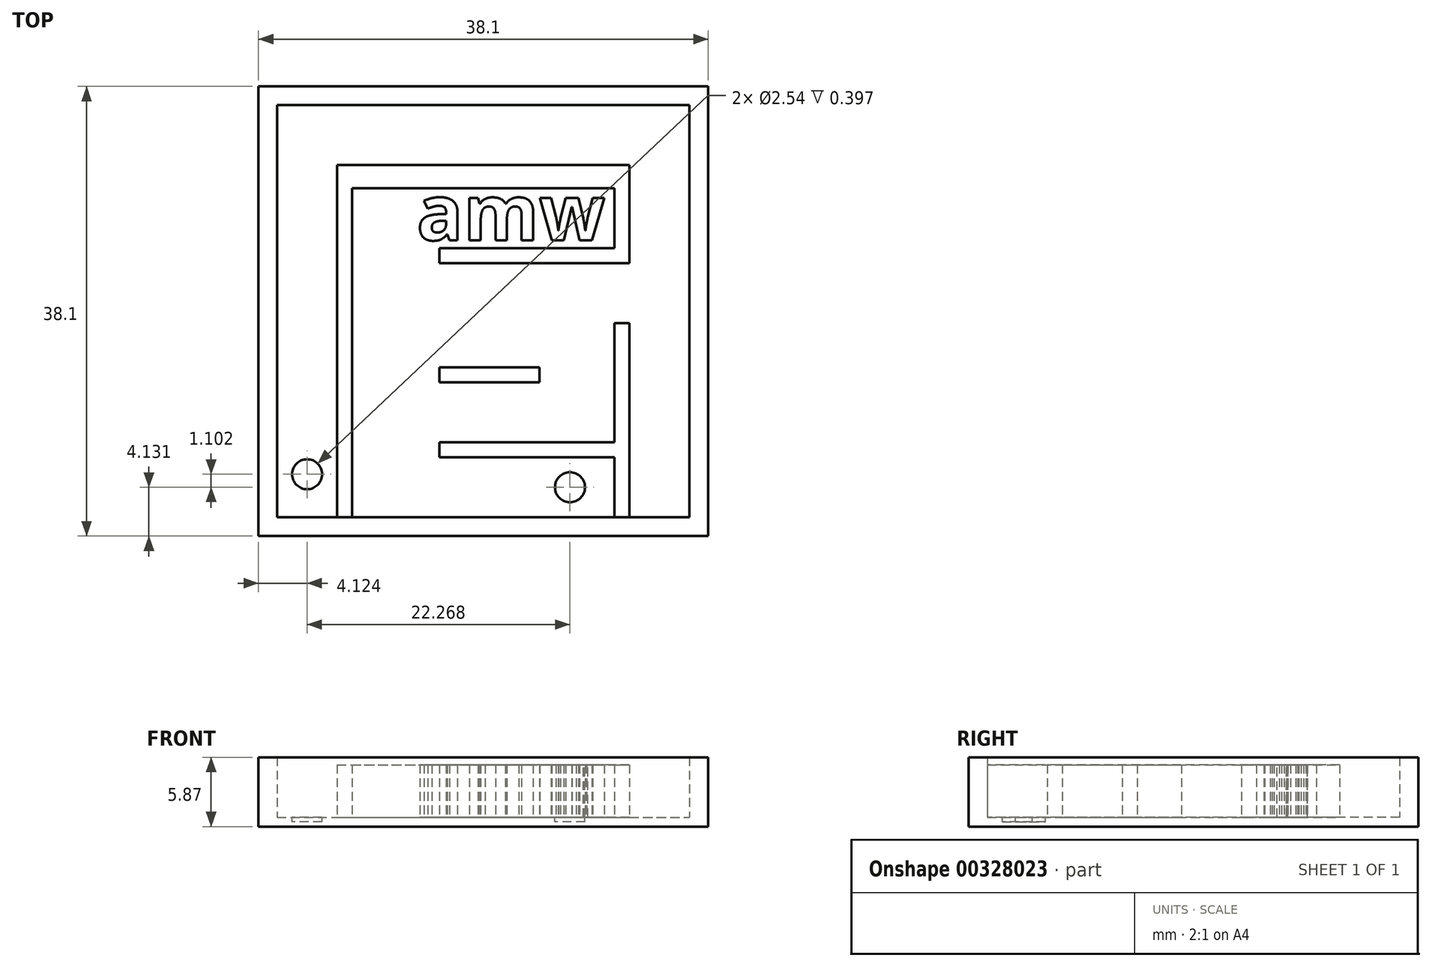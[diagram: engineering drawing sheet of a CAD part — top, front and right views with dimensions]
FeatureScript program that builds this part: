
annotation { "Feature Type Name" : "Feature", "Feature Type Description" : "" }
export const myFeature = defineFeature(function(context is Context, id is Id, definition is map)
    precondition{}
    {
        {
            var Q0;
            Q0=qCreatedBy(makeId("Top.planeOp"),FACE);
            var sketch = newSketch(context, id + "F0", { "sketchPlane" : qUnion([Q0])});
            skLineSegment(sketch, "E0.bottom", {"start": v(-17.87, 4.8) * mm, "end": v(20.23, 4.8) * mm});
            skLineSegment(sketch, "E0.top", {"start": v(-17.87, -33.3) * mm, "end": v(20.23, -33.3) * mm});
            skLineSegment(sketch, "E0.left", {"start": v(-17.87, 4.8) * mm, "end": v(-17.87, -33.3) * mm});
            skLineSegment(sketch, "E0.right", {"start": v(20.23, 4.8) * mm, "end": v(20.23, -33.3) * mm});
            skSolve(sketch);
        }
        {
            var Q0;
            Q0=makeQuery(id+"F0.imprint","IMPRINT",FACE,{"disambiguationData":[TD([[makeQuery(id+"F0.imprint","IMPRINT",EDGE,{"derivedFrom":sQuery(id+"F0.wireOp",EDGE,"E0.bottom")}),-1.0]])]});
            extrude(context, id + "F1", {"entities" : qUnion([Q0]), "depth" : 0.8 * mm});
        }
        {
            var Q0;
            Q0=makeQuery(id+"F1.opExtrude","CAP_FACE",FACE,{"disambiguationData":[OSD([sQuery(id+"F0.wireOp",EDGE,"E0.bottom"),sQuery(id+"F0.wireOp",EDGE,"E0.top"),sQuery(id+"F0.wireOp",EDGE,"E0.left"),sQuery(id+"F0.wireOp",EDGE,"E0.right")])],"isStart":false});
            var sketch = newSketch(context, id + "F2", { "sketchPlane" : qUnion([Q0])});
            skLineSegment(sketch, "E1.0", {"start": v(-16.29, 3.22) * mm, "end": v(18.64, 3.22) * mm});
            skLineSegment(sketch, "E1.1", {"start": v(-16.29, 3.22) * mm, "end": v(-16.29, -31.7) * mm});
            skLineSegment(sketch, "E1.2", {"start": v(-16.29, -31.7) * mm, "end": v(18.64, -31.7) * mm});
            skLineSegment(sketch, "E1.3", {"start": v(18.64, 3.22) * mm, "end": v(18.64, -31.7) * mm});
            skSolve(sketch);
        }
        {
            var Q0;
            Q0=makeQuery(id+"F2.imprint","IMPRINT",FACE,{"disambiguationData":[TD([[makeQuery(id+"F2.imprint","IMPRINT",EDGE,{"derivedFrom":sQuery(id+"F2.wireOp",EDGE,"E1.0")}),1.0]])]});
            extrude(context, id + "F3", {"entities" : qUnion([Q0]), "operationType" : NewBodyOperationType.ADD, "depth" : 5.08 * mm});
        }
        {
            var Q0;
            Q0=makeQuery(id+"F1.opExtrude","CAP_FACE",FACE,{"disambiguationData":[OSD([sQuery(id+"F0.wireOp",EDGE,"E0.bottom"),sQuery(id+"F0.wireOp",EDGE,"E0.top"),sQuery(id+"F0.wireOp",EDGE,"E0.left"),sQuery(id+"F0.wireOp",EDGE,"E0.right")])],"isStart":false});
            var sketch = newSketch(context, id + "F4", { "sketchPlane" : qUnion([Q0])});
            skLineSegment(sketch, "E2.bottom", {"start": v(-11.2, -31.7) * mm, "end": v(-9.94, -31.7) * mm});
            skLineSegment(sketch, "E2.top", {"start": v(-11.2, -1.86) * mm, "end": v(-9.94, -1.86) * mm});
            skLineSegment(sketch, "E2.left", {"start": v(-11.2, -31.7) * mm, "end": v(-11.2, -1.86) * mm});
            skLineSegment(sketch, "E3", {"start": v(-9.94, -1.86) * mm, "end": v(-9.94, -31.7) * mm});
            skLineSegment(sketch, "E4.left", {"start": v(13.56, -1.86) * mm, "end": v(13.56, -3.82) * mm});
            skPoint(sketch, "E5.oppositeSnap0", {"position": v(-11.2, -16.79) * mm});
            skLineSegment(sketch, "E5.right", {"start": v(-9.94, -20.38) * mm, "end": v(-9.94, -16.79) * mm});
            skLineSegment(sketch, "E6", {"start": v(-16.29, -31.7) * mm, "end": v(-11.2, -31.7) * mm});
            skCircle(sketch, "E7", {"center": v(-13.75, -28.07) * mm, "radius": 1.27 * mm});
            skPoint(sketch, "E7.centerSnap0", {"position": v(-13.75, -31.7) * mm});
            skPoint(sketch, "E8.orphan", {"position": v(-9.94, -1.86) * mm});
            skLineSegment(sketch, "E9.bottom", {"start": v(-9.94, -1.86) * mm, "end": v(13.56, -1.86) * mm});
            skLineSegment(sketch, "E9.top", {"start": v(-9.94, -3.82) * mm, "end": v(13.56, -3.82) * mm});
            skLineSegment(sketch, "E9.left", {"start": v(-9.94, -1.86) * mm, "end": v(-9.94, -3.82) * mm});
            skLineSegment(sketch, "E10", {"start": v(-9.94, -25.04) * mm, "end": v(-9.94, -31.7) * mm});
            skPoint(sketch, "E11.centerSnap0", {"position": v(-9.94, -28.38) * mm});
            skLineSegment(sketch, "E12.bottom", {"start": v(13.56, -1.86) * mm, "end": v(12.29, -1.86) * mm});
            skLineSegment(sketch, "E12.top", {"start": v(13.56, -10.17) * mm, "end": v(12.29, -10.17) * mm});
            skLineSegment(sketch, "E12.left", {"start": v(13.56, -1.86) * mm, "end": v(13.56, -10.17) * mm});
            skLineSegment(sketch, "E12.right", {"start": v(12.29, -1.86) * mm, "end": v(12.29, -10.17) * mm});
            skLineSegment(sketch, "E13.bottom", {"start": v(12.29, -31.7) * mm, "end": v(13.56, -31.7) * mm});
            skLineSegment(sketch, "E13.left", {"start": v(12.29, -31.7) * mm, "end": v(12.29, -26.63) * mm});
            skLineSegment(sketch, "E13.right", {"start": v(13.56, -31.7) * mm, "end": v(13.56, -25.36) * mm});
            skLineSegment(sketch, "E14.bottom", {"start": v(12.29, -10.17) * mm, "end": v(-2.54, -10.17) * mm});
            skLineSegment(sketch, "E14.top", {"start": v(12.29, -8.9) * mm, "end": v(-2.54, -8.9) * mm});
            skLineSegment(sketch, "E14.left", {"start": v(12.29, -10.17) * mm, "end": v(12.29, -8.9) * mm});
            skLineSegment(sketch, "E14.right", {"start": v(-2.54, -10.17) * mm, "end": v(-2.54, -8.9) * mm});
            skLineSegment(sketch, "E15.bottom", {"start": v(12.29, -25.36) * mm, "end": v(-2.54, -25.36) * mm});
            skLineSegment(sketch, "E15.top", {"start": v(12.29, -26.63) * mm, "end": v(-2.54, -26.63) * mm});
            skLineSegment(sketch, "E15.right", {"start": v(-2.54, -25.36) * mm, "end": v(-2.54, -26.63) * mm});
            skLineSegment(sketch, "E16", {"start": v(13.56, -15.25) * mm, "end": v(13.56, -25.36) * mm});
            skLineSegment(sketch, "E17.top", {"start": v(13.56, -15.25) * mm, "end": v(12.29, -15.25) * mm});
            skLineSegment(sketch, "E17.left", {"start": v(13.56, -25.36) * mm, "end": v(13.56, -15.25) * mm});
            skLineSegment(sketch, "E17.right", {"start": v(12.29, -25.36) * mm, "end": v(12.29, -15.25) * mm});
            skLineSegment(sketch, "E18.bottom", {"start": v(5.94, -25.36) * mm, "end": v(7.2, -25.36) * mm});
            skLineSegment(sketch, "E18.top", {"start": v(5.94, -15.25) * mm, "end": v(7.2, -15.25) * mm});
            skLineSegment(sketch, "E18.left", {"start": v(5.94, -25.36) * mm, "end": v(5.94, -15.25) * mm});
            skLineSegment(sketch, "E18.right", {"start": v(7.2, -25.36) * mm, "end": v(7.2, -15.25) * mm});
            skLineSegment(sketch, "E19.bottom", {"start": v(5.94, -19) * mm, "end": v(-2.54, -19) * mm});
            skLineSegment(sketch, "E19.top", {"start": v(5.94, -20.28) * mm, "end": v(-2.54, -20.28) * mm});
            skLineSegment(sketch, "E19.left", {"start": v(5.94, -19) * mm, "end": v(5.94, -20.28) * mm});
            skLineSegment(sketch, "E19.right", {"start": v(-2.54, -19) * mm, "end": v(-2.54, -20.28) * mm});
            skLineSegment(sketch, "E20.bottom", {"start": v(-2.54, -19) * mm, "end": v(0.86, -19) * mm});
            skCircle(sketch, "E21", {"center": v(8.52, -29.17) * mm, "radius": 1.27 * mm});
            skPoint(sketch, "E21.centerSnap0", {"position": v(12.29, -29.17) * mm});
            skSolve(sketch);
        }
        {
            var Q0;
            {var subQ0=sQuery(id+"F4.wireOp",EDGE,"E9.bottom");Q0=makeQuery(id+"F4.imprint","IMPRINT",FACE,{"disambiguationData":[TD([[makeQuery(id+"F4.imprint","IMPRINT",EDGE,{"derivedFrom":subQ0}),-1.0]])]});}
            var Q1;
            {var subQ6=sQuery(id+"F4.wireOp",EDGE,"E12.top");Q1=makeQuery(id+"F4.imprint","IMPRINT",FACE,{"disambiguationData":[TD([[makeQuery(id+"F4.imprint","IMPRINT",EDGE,{"derivedFrom":subQ6}),-1.0]])]});}
            var Q2;
            {var subQ5=sQuery(id+"F4.wireOp",EDGE,"E12.bottom");Q2=makeQuery(id+"F4.imprint","IMPRINT",FACE,{"disambiguationData":[TD([[makeQuery(id+"F4.imprint","IMPRINT",EDGE,{"derivedFrom":subQ5}),1.0]])]});}
            var Q3;
            Q3=makeQuery(id+"F4.imprint","IMPRINT",FACE,{"disambiguationData":[TD([[makeQuery(id+"F4.imprint","IMPRINT",EDGE,{"derivedFrom":sQuery(id+"F4.wireOp",EDGE,"E14.bottom")}),-1.0]])]});
            var Q4;
            Q4=makeQuery(id+"F4.imprint","IMPRINT",FACE,{"disambiguationData":[TD([[makeQuery(id+"F4.imprint","IMPRINT",EDGE,{"derivedFrom":sQuery(id+"F4.wireOp",EDGE,"E2.bottom")}),1.0]])]});
            var Q5;
            Q5=makeQuery(id+"F4.imprint","IMPRINT",FACE,{"disambiguationData":[TD([[makeQuery(id+"F4.imprint","IMPRINT",EDGE,{"derivedFrom":sQuery(id+"F4.wireOp",EDGE,"E19.bottom")}),1.0]])]});
            var Q6;
            {var subQ3=sQuery(id+"F4.wireOp",EDGE,"E18.bottom");Q6=makeQuery(id+"F4.imprint","IMPRINT",FACE,{"disambiguationData":[TD([[makeQuery(id+"F4.imprint","IMPRINT",EDGE,{"derivedFrom":subQ3}),1.0]])]});}
            var Q7;
            Q7=makeQuery(id+"F4.imprint","IMPRINT",FACE,{"disambiguationData":[TD([[makeQuery(id+"F4.imprint","IMPRINT",EDGE,{"derivedFrom":sQuery(id+"F4.wireOp",EDGE,"E13.bottom")}),1.0]])]});
            extrude(context, id + "F5", {"entities" : qUnion([Q0, Q1, Q2, Q3, Q4, Q5, Q6, Q7]), "operationType" : NewBodyOperationType.ADD, "depth" : 4.44 * mm});
        }
        {
            var Q0;
            Q0=makeQuery(id+"F4.imprint","IMPRINT",FACE,{"disambiguationData":[TD([[makeQuery(id+"F4.imprint","IMPRINT",EDGE,{"derivedFrom":sQuery(id+"F4.wireOp",EDGE,"E7")}),1.0]])]});
            var Q1;
            Q1=makeQuery(id+"F4.imprint","IMPRINT",FACE,{"disambiguationData":[TD([[makeQuery(id+"F4.imprint","IMPRINT",EDGE,{"derivedFrom":sQuery(id+"F4.wireOp",EDGE,"E21")}),1.0]])]});
            extrude(context, id + "F6", {"entities" : qUnion([Q0, Q1]), "operationType" : NewBodyOperationType.REMOVE, "oppositeDirection" : true, "depth" : 0.4 * mm});
        }
        {
            var Q0;
            Q0=makeQuery(id+"F2.imprint","IMPRINT",FACE,{"disambiguationData":[TD([[makeQuery(id+"F2.imprint","IMPRINT",EDGE,{"derivedFrom":sQuery(id+"F2.wireOp",EDGE,"E1.0")}),-1.0]])]});
            var sketch = newSketch(context, id + "F7", { "sketchPlane" : qUnion([Q0])});
            skText(sketch, "E22", { "text": "amw\n", "fontName": "OpenSans-Bold.ttf"});
            const initialGuessF7  = {"E22": [-0.00446, -0.00823, 1, 0, 0.0047]};
            skSetInitialGuess(sketch, initialGuessF7);
            skSolve(sketch);
        }
        {
            var Q0;
            Q0 = qSketchRegion(id + "F7", true);
            extrude(context, id + "F8", {"entities" : qUnion([Q0]), "operationType" : NewBodyOperationType.ADD, "depth" : 4.44 * mm});
        }
    });
